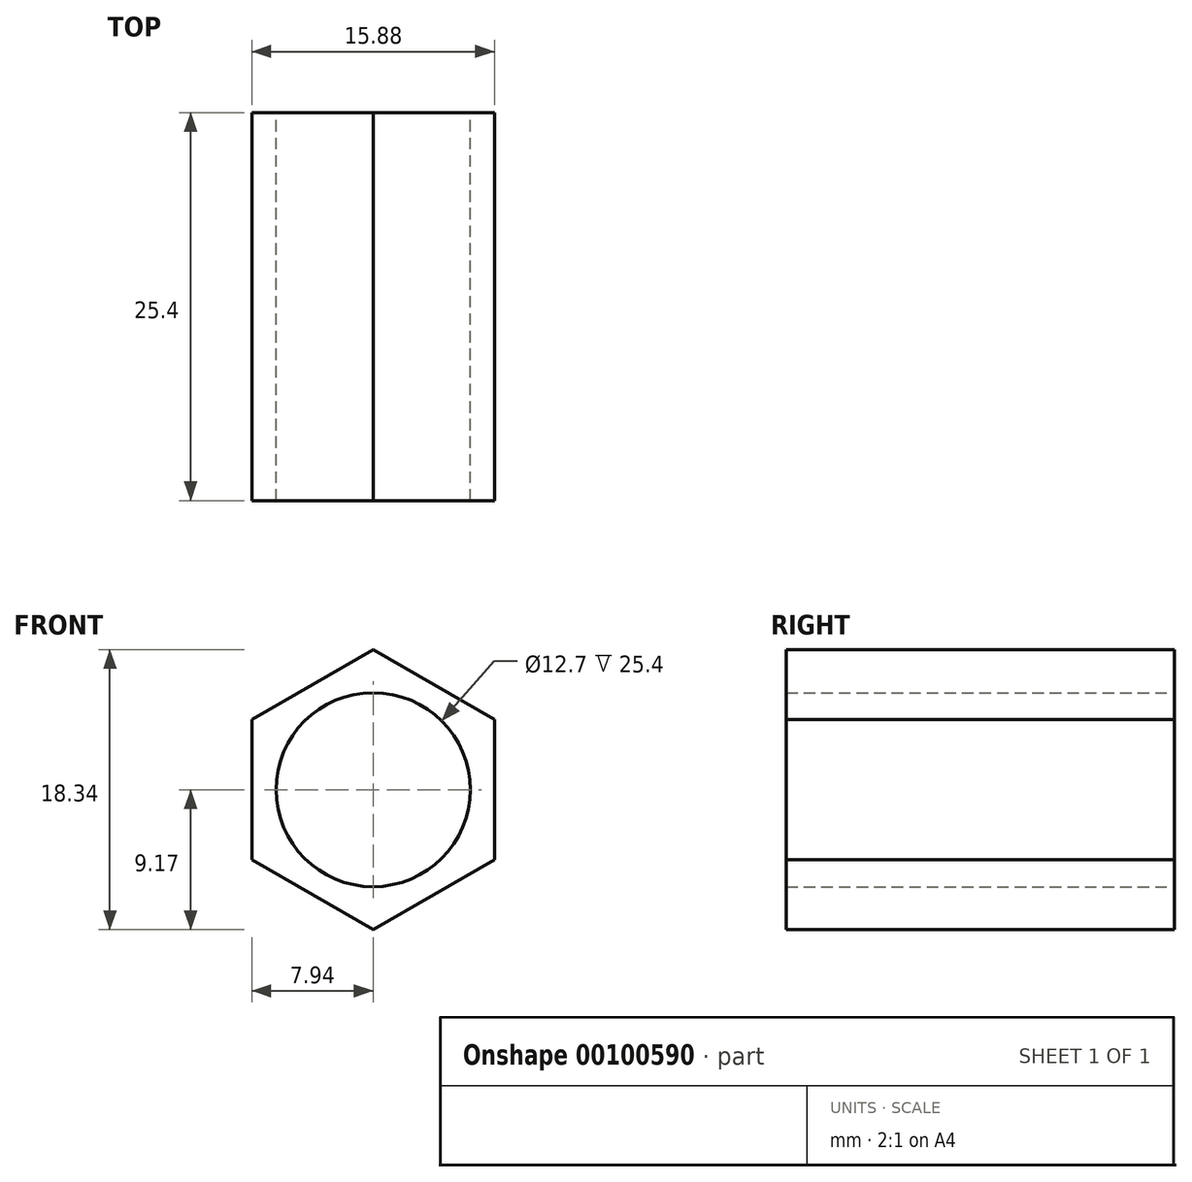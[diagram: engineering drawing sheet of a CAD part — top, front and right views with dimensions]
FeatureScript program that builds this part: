
annotation { "Feature Type Name" : "Feature", "Feature Type Description" : "" }
export const myFeature = defineFeature(function(context is Context, id is Id, definition is map)
    precondition{}
    {
        {
            var Q0;
            Q0=qCreatedBy(makeId("Front.planeOp"),FACE);
            var sketch = newSketch(context, id + "F0", { "sketchPlane" : qUnion([Q0])});
            skCircle(sketch, "E0.cCircle", {"center": v(0, 0) * mm, "radius": 7.94 * mm, "construction": true});
            skLineSegment(sketch, "E0.0", {"start": v(-7.94, -4.58) * mm, "end": v(-7.94, 4.58) * mm});
            skLineSegment(sketch, "E0.1", {"start": v(-7.94, 4.58) * mm, "end": v(0, 9.17) * mm});
            skLineSegment(sketch, "E0.2", {"start": v(0, 9.17) * mm, "end": v(7.94, 4.58) * mm});
            skLineSegment(sketch, "E0.3", {"start": v(7.94, 4.58) * mm, "end": v(7.94, -4.58) * mm});
            skLineSegment(sketch, "E0.4", {"start": v(7.94, -4.58) * mm, "end": v(0, -9.17) * mm});
            skLineSegment(sketch, "E0.5", {"start": v(0, -9.17) * mm, "end": v(-7.94, -4.58) * mm});
            skPoint(sketch, "E0.0.midPoint", {"position": v(-7.94, 0) * mm});
            skCircle(sketch, "E1", {"center": v(0, 0) * mm, "radius": 6.35 * mm});
            skSolve(sketch);
        }
        {
            var Q0;
            Q0 = qSketchRegion(id + "F0", true);
            extrude(context, id + "F1", {"entities" : qUnion([Q0]), "depth" : 25.4 * mm});
        }
    });
